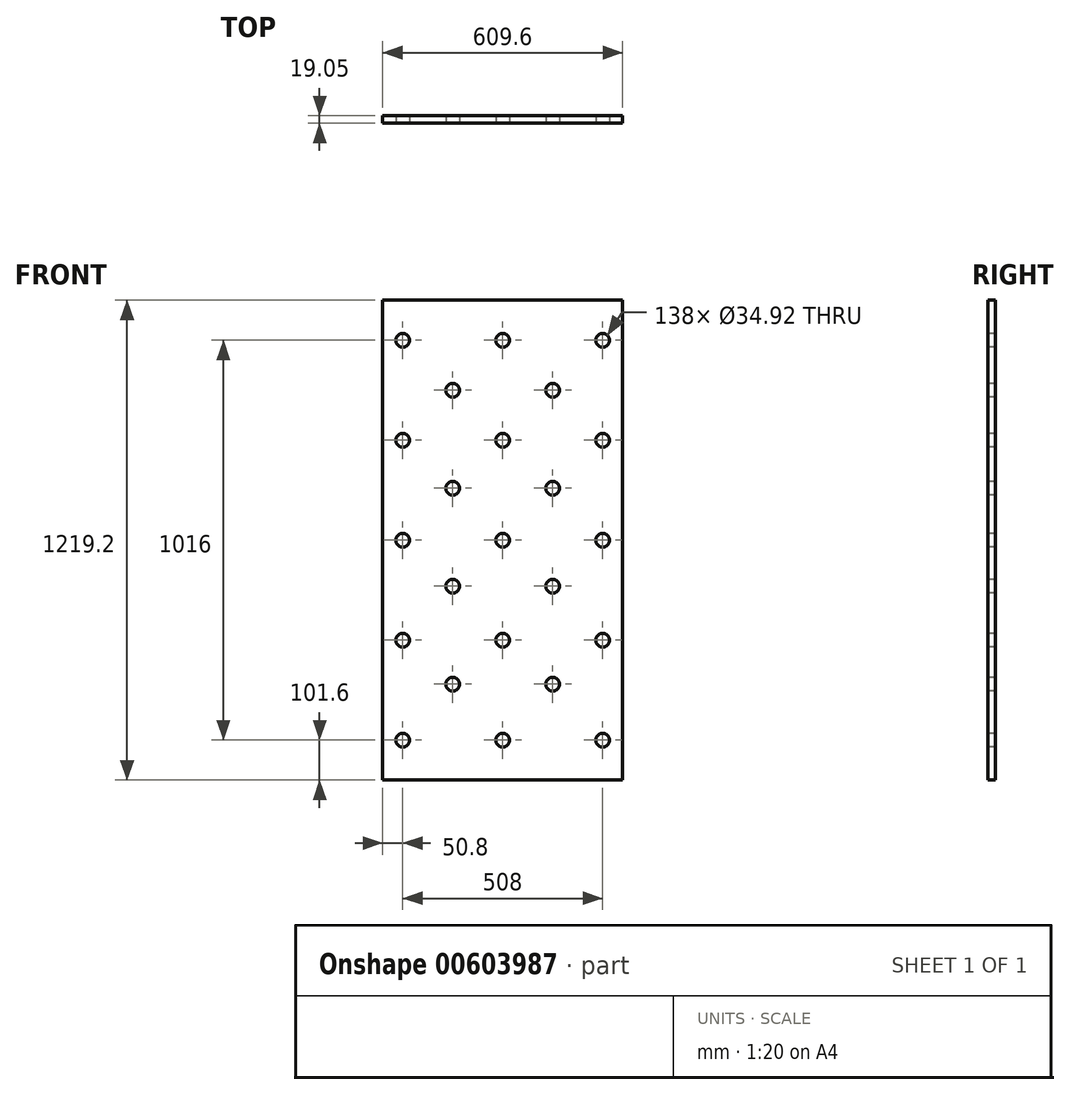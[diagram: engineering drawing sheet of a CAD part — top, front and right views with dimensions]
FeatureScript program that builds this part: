
annotation { "Feature Type Name" : "Feature", "Feature Type Description" : "" }
export const myFeature = defineFeature(function(context is Context, id is Id, definition is map)
    precondition{}
    {
        {
            var Q0;
            Q0=qCreatedBy(makeId("Front.planeOp"),FACE);
            var sketch = newSketch(context, id + "F0", { "sketchPlane" : qUnion([Q0])});
            skLineSegment(sketch, "E0.bottom", {"start": v(304.8, -609.6) * mm, "end": v(-304.8, -609.6) * mm});
            skLineSegment(sketch, "E0.top", {"start": v(304.8, 609.6) * mm, "end": v(-304.8, 609.6) * mm});
            skLineSegment(sketch, "E0.left", {"start": v(304.8, -609.6) * mm, "end": v(304.8, 609.6) * mm});
            skLineSegment(sketch, "E0.right", {"start": v(-304.8, -609.6) * mm, "end": v(-304.8, 609.6) * mm});
            skPoint(sketch, "E0.middle", {"position": v(0, 0) * mm});
            skSolve(sketch);
        }
        {
            var Q0;
            Q0=makeQuery(id+"F0.imprint","IMPRINT",FACE,{"disambiguationData":[TD([[makeQuery(id+"F0.imprint","IMPRINT",EDGE,{"derivedFrom":sQuery(id+"F0.wireOp",EDGE,"E0.bottom")}),-1.0]])]});
            extrude(context, id + "F1", {"entities" : qUnion([Q0]), "depth" : 19.05 * mm, "offsetDistance" : 25.4 * mm});
        }
        {
            var Q0;
            Q0=makeQuery(id+"F1.opExtrude","CAP_FACE",FACE,{"disambiguationData":[OSD([sQuery(id+"F0.wireOp",EDGE,"E0.bottom"),sQuery(id+"F0.wireOp",EDGE,"E0.top"),sQuery(id+"F0.wireOp",EDGE,"E0.left"),sQuery(id+"F0.wireOp",EDGE,"E0.right")])],"isStart":false});
            var sketch = newSketch(context, id + "F2", { "sketchPlane" : qUnion([Q0])});
            skCircle(sketch, "E1", {"center": v(-254, 508) * mm, "radius": 17.46 * mm});
            skCircle(sketch, "E2.0.1.0", {"center": v(-254, 254) * mm, "radius": 17.46 * mm});
            skCircle(sketch, "E2.0.2.0", {"center": v(-254, 0) * mm, "radius": 17.46 * mm});
            skCircle(sketch, "E2.0.3.0", {"center": v(-254, -254) * mm, "radius": 17.46 * mm});
            skCircle(sketch, "E2.0.4.0", {"center": v(-254, -508) * mm, "radius": 17.46 * mm});
            skCircle(sketch, "E2.1.0.0", {"center": v(0, 508) * mm, "radius": 17.46 * mm});
            skCircle(sketch, "E2.1.1.0", {"center": v(0, 254) * mm, "radius": 17.46 * mm});
            skCircle(sketch, "E2.1.2.0", {"center": v(0, 0) * mm, "radius": 17.46 * mm});
            skCircle(sketch, "E2.1.3.0", {"center": v(0, -254) * mm, "radius": 17.46 * mm});
            skCircle(sketch, "E2.1.4.0", {"center": v(0, -508) * mm, "radius": 17.46 * mm});
            skCircle(sketch, "E2.2.0.0", {"center": v(254, 508) * mm, "radius": 17.46 * mm});
            skCircle(sketch, "E2.2.1.0", {"center": v(254, 254) * mm, "radius": 17.46 * mm});
            skCircle(sketch, "E2.2.2.0", {"center": v(254, 0) * mm, "radius": 17.46 * mm});
            skCircle(sketch, "E2.2.3.0", {"center": v(254, -254) * mm, "radius": 17.46 * mm});
            skCircle(sketch, "E2.2.4.0", {"center": v(254, -508) * mm, "radius": 17.46 * mm});
            skLineSegment(sketch, "E2.direction1", {"start": v(-254, 508) * mm, "end": v(0, 508) * mm, "construction": true});
            skLineSegment(sketch, "E2.direction2", {"start": v(-254, 508) * mm, "end": v(-254, 254) * mm, "construction": true});
            skCircle(sketch, "E3", {"center": v(-127, 381) * mm, "radius": 17.46 * mm});
            skCircle(sketch, "E4.0.1.0", {"center": v(-127, 132.08) * mm, "radius": 17.46 * mm});
            skCircle(sketch, "E4.0.2.0", {"center": v(-127, -116.84) * mm, "radius": 17.46 * mm});
            skCircle(sketch, "E4.0.3.0", {"center": v(-127, -365.76) * mm, "radius": 17.46 * mm});
            skCircle(sketch, "E4.1.0.0", {"center": v(127, 381) * mm, "radius": 17.46 * mm});
            skCircle(sketch, "E4.1.1.0", {"center": v(127, 132.08) * mm, "radius": 17.46 * mm});
            skCircle(sketch, "E4.1.2.0", {"center": v(127, -116.84) * mm, "radius": 17.46 * mm});
            skCircle(sketch, "E4.1.3.0", {"center": v(127, -365.76) * mm, "radius": 17.46 * mm});
            skLineSegment(sketch, "E4.direction1", {"start": v(-127, 381) * mm, "end": v(127, 381) * mm, "construction": true});
            skLineSegment(sketch, "E4.direction2", {"start": v(-127, 381) * mm, "end": v(-127, 132.08) * mm, "construction": true});
            skSolve(sketch);
        }
        {
            var Q0;
            Q0 = qSketchRegion(id + "F2", true);
            extrude(context, id + "F3", {"entities" : qUnion([Q0]), "operationType" : NewBodyOperationType.REMOVE, "endBound" : BoundingType.THROUGH_ALL, "oppositeDirection" : true, "depth" : 25.4 * mm, "offsetDistance" : 25.4 * mm});
        }
    });
